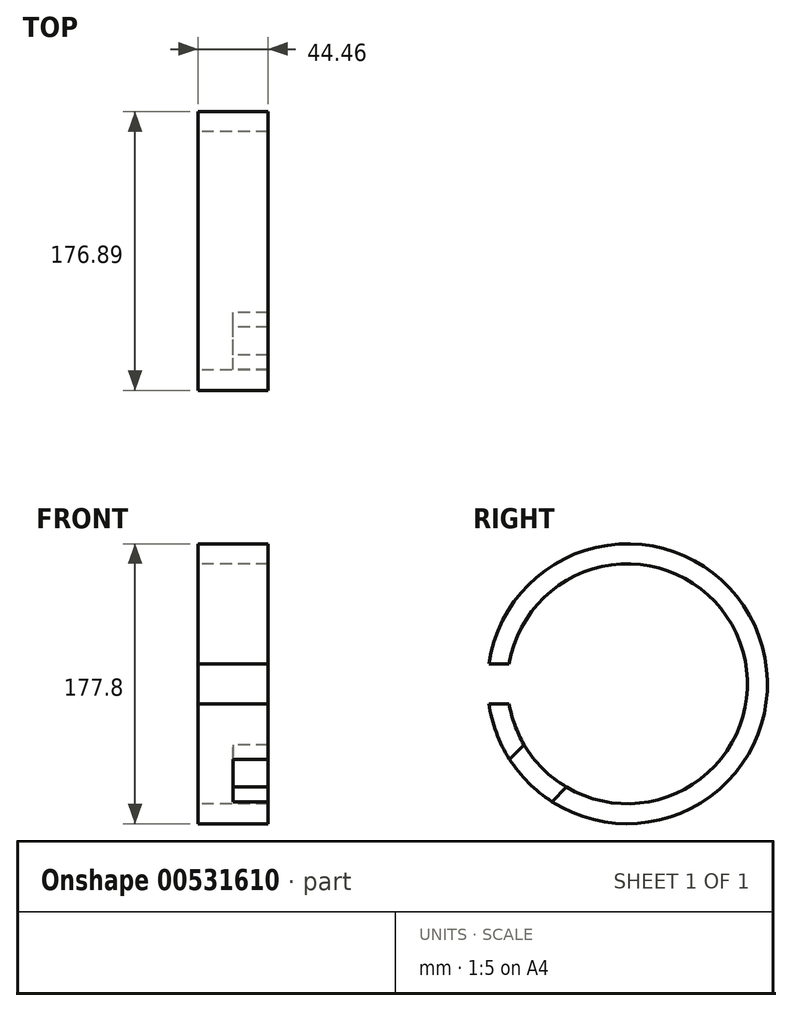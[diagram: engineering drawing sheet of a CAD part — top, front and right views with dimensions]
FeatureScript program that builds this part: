
annotation { "Feature Type Name" : "Feature", "Feature Type Description" : "" }
export const myFeature = defineFeature(function(context is Context, id is Id, definition is map)
    precondition{}
    {
        {
            var Q0;
            Q0=qCreatedBy(makeId("Front.planeOp"),FACE);
            var sketch = newSketch(context, id + "F0", { "sketchPlane" : qUnion([Q0])});
            skLineSegment(sketch, "E0", {"start": v(-22.22, 88.9) * mm, "end": v(-22.22, 76.2) * mm});
            skLineSegment(sketch, "E1", {"start": v(-22.22, 76.2) * mm, "end": v(22.22, 76.2) * mm});
            skLineSegment(sketch, "E2", {"start": v(22.23, 76.2) * mm, "end": v(22.23, 88.9) * mm});
            skLineSegment(sketch, "E3", {"start": v(22.22, 88.9) * mm, "end": v(-22.22, 88.9) * mm});
            skPoint(sketch, "E4", {"position": v(0, 88.9) * mm});
            skLineSegment(sketch, "E5", {"start": v(-22.22, 0) * mm, "end": v(22.22, 0) * mm});
            skSolve(sketch);
        }
        {
            var Q0;
            Q0=qSketchRegion(id+"F0",true);
            var Q1;
            Q1=sQuery(id+"F0.wireOp",EDGE,"E5");
            revolve(context, id + "F1", {"entities" : qUnion([Q0]), "axis" : qUnion([Q1]), "revolveType" : RevolveType.FULL});
        }
        {
            var Q0;
            Q0=qCreatedBy(makeId("Front.planeOp"),FACE);
            var sketch = newSketch(context, id + "F2", { "sketchPlane" : qUnion([Q0])});
            skLineSegment(sketch, "E6", {"start": v(-31.75, 12.7) * mm, "end": v(31.75, 12.7) * mm});
            skLineSegment(sketch, "E7", {"start": v(31.75, 12.7) * mm, "end": v(31.75, -12.7) * mm});
            skLineSegment(sketch, "E8", {"start": v(31.75, -12.7) * mm, "end": v(-31.75, -12.7) * mm});
            skLineSegment(sketch, "E9", {"start": v(-31.75, -12.7) * mm, "end": v(-31.75, 12.7) * mm});
            skPoint(sketch, "E10", {"position": v(0, -12.7) * mm});
            skLineSegment(sketch, "E11", {"start": v(0, 12.7) * mm, "end": v(0, -12.7) * mm});
            skSolve(sketch);
        }
        {
            var Q0;
            {var subQ0=sQuery(id+"F2.wireOp",EDGE,"E7");Q0=makeQuery(id+"F2.imprint","IMPRINT",FACE,{"disambiguationData":[TD([[makeQuery(id+"F2.imprint","IMPRINT",EDGE,{"derivedFrom":subQ0}),-1.0]])]});}
            var Q1;
            {var subQ0=sQuery(id+"F2.wireOp",EDGE,"E9");Q1=makeQuery(id+"F2.imprint","IMPRINT",FACE,{"disambiguationData":[TD([[makeQuery(id+"F2.imprint","IMPRINT",EDGE,{"derivedFrom":subQ0}),-1.0]])]});}
            extrude(context, id + "F3", {"entities" : qUnion([Q0, Q1]), "operationType" : NewBodyOperationType.REMOVE, "endBound" : BoundingType.THROUGH_ALL, "depth" : 25.4 * mm});
        }
        {
            var Q0;
            Q0=qCreatedBy(makeId("Front.planeOp"),FACE);
            var Q1;
            Q1=qCreatedBy(makeId("Top.planeOp"),FACE);
            cPlane(context, id + "F4", {"entities" : qUnion([Q0, Q1]), "cplaneType" : CPlaneType.MID_PLANE, "offset" : 25.4 * mm, "width" : 152.4 * mm, "height" : 152.4 * mm});
        }
        {
            var Q0;
            Q0=qCreatedBy(id+"F4.planeOp",FACE);
            var sketch = newSketch(context, id + "F5", { "sketchPlane" : qUnion([Q0])});
            skLineSegment(sketch, "E12", {"start": v(0, 19.05) * mm, "end": v(0, -19.05) * mm});
            skLineSegment(sketch, "E13", {"start": v(0, -19.05) * mm, "end": v(22.23, -19.05) * mm});
            skLineSegment(sketch, "E14", {"start": v(22.23, -19.05) * mm, "end": v(22.23, 19.05) * mm});
            skLineSegment(sketch, "E15", {"start": v(22.23, 19.05) * mm, "end": v(0, 19.05) * mm});
            skSolve(sketch);
        }
        {
            var Q0;
            Q0=makeQuery(id+"F5.imprint","IMPRINT",FACE,{"disambiguationData":[TD([[makeQuery(id+"F5.imprint","IMPRINT",EDGE,{"derivedFrom":sQuery(id+"F5.wireOp",EDGE,"E12")}),1.0]])]});
            extrude(context, id + "F6", {"entities" : qUnion([Q0]), "operationType" : NewBodyOperationType.REMOVE, "endBound" : BoundingType.THROUGH_ALL, "depth" : 25.4 * mm});
        }
    });
